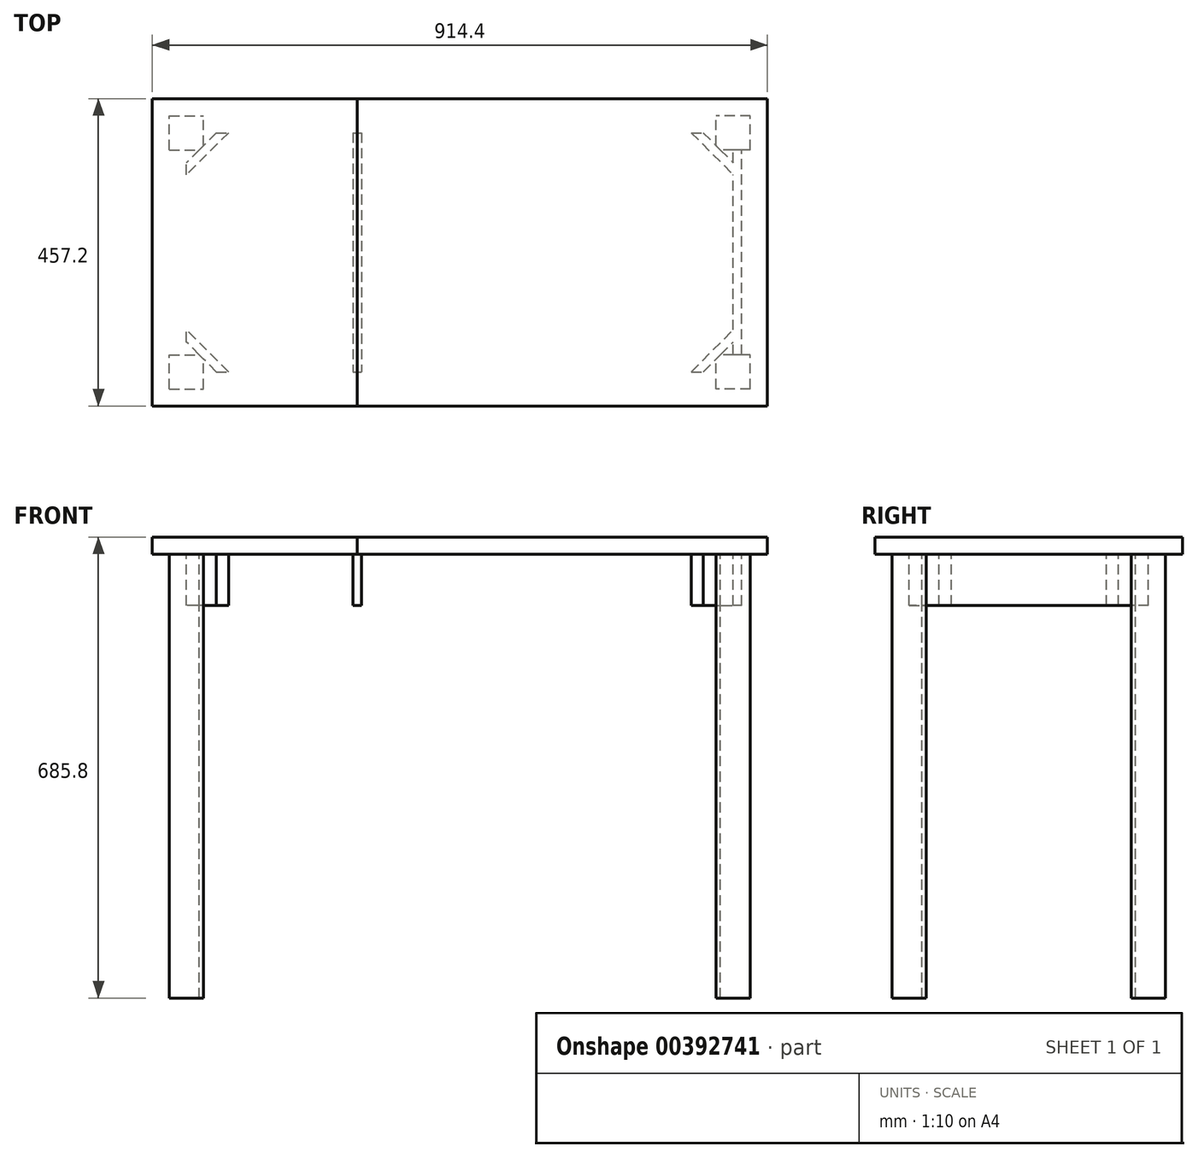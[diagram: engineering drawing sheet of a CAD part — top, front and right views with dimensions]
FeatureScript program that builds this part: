
annotation { "Feature Type Name" : "Feature", "Feature Type Description" : "" }
export const myFeature = defineFeature(function(context is Context, id is Id, definition is map)
    precondition{}
    {
        {
            var Q0;
            Q0=qCreatedBy(makeId("Top.planeOp"),FACE);
            var sketch = newSketch(context, id + "F0", { "sketchPlane" : qUnion([Q0])});
            skLineSegment(sketch, "E0.bottom", {"start": v(-394.13, 238.74) * mm, "end": v(215.47, 238.74) * mm});
            skLineSegment(sketch, "E0.top", {"start": v(-394.13, -218.46) * mm, "end": v(215.47, -218.46) * mm});
            skLineSegment(sketch, "E0.left", {"start": v(-394.13, 238.74) * mm, "end": v(-394.13, -218.46) * mm});
            skLineSegment(sketch, "E0.right", {"start": v(215.47, 238.74) * mm, "end": v(215.47, -218.46) * mm});
            skLineSegment(sketch, "E1.bottom", {"start": v(-394.13, 238.74) * mm, "end": v(-698.93, 238.74) * mm});
            skLineSegment(sketch, "E1.top", {"start": v(-394.13, -218.46) * mm, "end": v(-698.93, -218.46) * mm});
            skLineSegment(sketch, "E1.right", {"start": v(-698.93, 238.74) * mm, "end": v(-698.93, -218.46) * mm});
            skSolve(sketch);
        }
        {
            var Q0;
            Q0=makeQuery(id+"F0.imprint","IMPRINT",FACE,{"disambiguationData":[TD([[makeQuery(id+"F0.imprint","IMPRINT",EDGE,{"derivedFrom":sQuery(id+"F0.wireOp",EDGE,"E0.bottom")}),-1.0]])]});
            extrude(context, id + "F1", {"entities" : qUnion([Q0]), "depth" : 25.4 * mm});
        }
        {
            var Q0;
            Q0=makeQuery(id+"F0.imprint","IMPRINT",FACE,{"disambiguationData":[TD([[makeQuery(id+"F0.imprint","IMPRINT",EDGE,{"derivedFrom":sQuery(id+"F0.wireOp",EDGE,"E1.bottom")}),1.0]])]});
            extrude(context, id + "F2", {"entities" : qUnion([Q0]), "depth" : 25.4 * mm});
        }
        {
            var Q0;
            Q0=makeQuery(id+"F0.imprint","IMPRINT",FACE,{"disambiguationData":[TD([[makeQuery(id+"F0.imprint","IMPRINT",EDGE,{"derivedFrom":sQuery(id+"F0.wireOp",EDGE,"E0.bottom")}),-1.0]])]});
            var sketch = newSketch(context, id + "F3", { "sketchPlane" : qUnion([Q0])});
            skLineSegment(sketch, "E2.bottom", {"start": v(-673.53, -193.06) * mm, "end": v(-622.73, -193.06) * mm});
            skLineSegment(sketch, "E2.top", {"start": v(-673.53, -142.26) * mm, "end": v(-622.73, -142.26) * mm});
            skLineSegment(sketch, "E2.left", {"start": v(-673.53, -193.06) * mm, "end": v(-673.53, -142.26) * mm});
            skLineSegment(sketch, "E2.right", {"start": v(-622.73, -193.06) * mm, "end": v(-622.73, -142.26) * mm});
            skLineSegment(sketch, "E3.bottom", {"start": v(-673.53, 162.54) * mm, "end": v(-622.73, 162.54) * mm});
            skLineSegment(sketch, "E3.top", {"start": v(-673.53, 213.34) * mm, "end": v(-622.73, 213.34) * mm});
            skLineSegment(sketch, "E3.left", {"start": v(-673.53, 162.54) * mm, "end": v(-673.53, 213.34) * mm});
            skLineSegment(sketch, "E3.right", {"start": v(-622.73, 162.54) * mm, "end": v(-622.73, 213.34) * mm});
            skLineSegment(sketch, "E4.bottom", {"start": v(-648.13, -142.26) * mm, "end": v(-660.83, -142.26) * mm});
            skLineSegment(sketch, "E4.top", {"start": v(-648.13, 162.54) * mm, "end": v(-660.83, 162.54) * mm});
            skLineSegment(sketch, "E4.left", {"start": v(-648.13, -142.26) * mm, "end": v(-648.13, 162.54) * mm});
            skLineSegment(sketch, "E4.right", {"start": v(-660.83, -142.26) * mm, "end": v(-660.83, 162.54) * mm});
            skLineSegment(sketch, "E5", {"start": v(-241.73, -218.46) * mm, "end": v(-241.73, 238.74) * mm, "construction": true});
            skLineSegment(sketch, "E6.MirrorCS", {"start": v(190.07, -193.06) * mm, "end": v(139.27, -193.06) * mm});
            skLineSegment(sketch, "E7.MirrorCS", {"start": v(190.07, -193.06) * mm, "end": v(190.07, -142.26) * mm});
            skLineSegment(sketch, "E8.MirrorCS", {"start": v(190.07, -142.26) * mm, "end": v(139.27, -142.26) * mm});
            skLineSegment(sketch, "E9.MirrorCS", {"start": v(139.27, -193.06) * mm, "end": v(139.27, -142.26) * mm});
            skLineSegment(sketch, "E10.MirrorCS", {"start": v(164.67, -142.26) * mm, "end": v(164.67, 162.54) * mm});
            skLineSegment(sketch, "E11.MirrorCS", {"start": v(177.37, -142.26) * mm, "end": v(177.37, 162.54) * mm});
            skLineSegment(sketch, "E12.MirrorCS", {"start": v(190.07, 162.54) * mm, "end": v(139.27, 162.54) * mm});
            skLineSegment(sketch, "E13.MirrorCS", {"start": v(139.27, 162.54) * mm, "end": v(139.27, 213.34) * mm});
            skLineSegment(sketch, "E14.MirrorCS", {"start": v(190.07, 213.34) * mm, "end": v(139.27, 213.34) * mm});
            skLineSegment(sketch, "E15.MirrorCS", {"start": v(190.07, 162.54) * mm, "end": v(190.07, 213.34) * mm});
            skLineSegment(sketch, "E16", {"start": v(-622.73, -167.66) * mm, "end": v(-241.73, -167.66) * mm});
            skLineSegment(sketch, "E17", {"start": v(-241.73, -167.66) * mm, "end": v(139.27, -167.66) * mm});
            skLineSegment(sketch, "E18", {"start": v(139.27, -167.66) * mm, "end": v(139.27, -180.36) * mm});
            skLineSegment(sketch, "E19", {"start": v(139.27, -180.36) * mm, "end": v(-622.73, -180.36) * mm});
            skLineSegment(sketch, "E20", {"start": v(-622.73, -180.36) * mm, "end": v(-622.73, -167.66) * mm});
            skLineSegment(sketch, "E21", {"start": v(-603.68, -167.66) * mm, "end": v(-648.13, -123.2) * mm});
            skLineSegment(sketch, "E22", {"start": v(-585.72, -167.66) * mm, "end": v(-648.13, -105.25) * mm});
            skLineSegment(sketch, "E23.MirrorCS", {"start": v(102.26, -167.66) * mm, "end": v(164.67, -105.25) * mm});
            skLineSegment(sketch, "E24.MirrorCS", {"start": v(120.22, -167.66) * mm, "end": v(164.67, -123.2) * mm});
            skPoint(sketch, "E25", {"position": v(-622.73, -148.6) * mm});
            skPoint(sketch, "E26", {"position": v(-629.08, -142.26) * mm});
            skLineSegment(sketch, "E27.bottom", {"start": v(-622.73, 187.94) * mm, "end": v(139.27, 187.94) * mm});
            skLineSegment(sketch, "E27.top", {"start": v(-622.73, 200.64) * mm, "end": v(139.27, 200.64) * mm});
            skLineSegment(sketch, "E27.left", {"start": v(-622.73, 187.94) * mm, "end": v(-622.73, 200.64) * mm});
            skLineSegment(sketch, "E27.right", {"start": v(139.27, 187.94) * mm, "end": v(139.27, 200.64) * mm});
            skLineSegment(sketch, "E28", {"start": v(215.47, 10.14) * mm, "end": v(-698.93, 10.14) * mm, "construction": true});
            skLineSegment(sketch, "E29.MirrorCS", {"start": v(102.26, 187.94) * mm, "end": v(164.67, 125.53) * mm});
            skLineSegment(sketch, "E30.MirrorCS", {"start": v(120.22, 187.94) * mm, "end": v(164.67, 143.5) * mm});
            skLineSegment(sketch, "E31.MirrorCS", {"start": v(-585.72, 187.94) * mm, "end": v(-648.13, 125.53) * mm});
            skLineSegment(sketch, "E32.MirrorCS", {"start": v(-603.68, 187.94) * mm, "end": v(-648.13, 143.5) * mm});
            skLineSegment(sketch, "E33.bottom", {"start": v(-400.91, 187.94) * mm, "end": v(-388.21, 187.94) * mm});
            skLineSegment(sketch, "E33.top", {"start": v(-400.91, -167.66) * mm, "end": v(-388.21, -167.66) * mm});
            skLineSegment(sketch, "E33.left", {"start": v(-400.91, 187.94) * mm, "end": v(-400.91, -167.66) * mm});
            skLineSegment(sketch, "E33.right", {"start": v(-388.21, 187.94) * mm, "end": v(-388.21, -167.66) * mm});
            skSolve(sketch);
        }
        {
            var Q0;
            {var subQ0=sQuery(id+"F3.wireOp",EDGE,"E18");Q0=makeQuery(id+"F3.imprint","IMPRINT",FACE,{"disambiguationData":[TD([[makeQuery(id+"F3.imprint","IMPRINT",EDGE,{"derivedFrom":subQ0}),-1.0]])]});}
            var Q1;
            {var subQ0=sQuery(id+"F3.wireOp",EDGE,"E20");Q1=makeQuery(id+"F3.imprint","IMPRINT",FACE,{"disambiguationData":[TD([[makeQuery(id+"F3.imprint","IMPRINT",EDGE,{"derivedFrom":subQ0}),-1.0]])]});}
            var Q2;
            {var subQ3=sQuery(id+"F3.wireOp",EDGE,"E22");Q2=makeQuery(id+"F3.imprint","IMPRINT",FACE,{"disambiguationData":[TD([[makeQuery(id+"F3.imprint","IMPRINT",EDGE,{"derivedFrom":subQ3}),1.0]])]});}
            var Q3;
            {var subQ3=sQuery(id+"F3.wireOp",EDGE,"E4.bottom");Q3=makeQuery(id+"F3.imprint","IMPRINT",FACE,{"disambiguationData":[TD([[makeQuery(id+"F3.imprint","IMPRINT",EDGE,{"derivedFrom":subQ3}),-1.0]])]});}
            var Q4;
            {var subQ0=sQuery(id+"F3.wireOp",EDGE,"E31.MirrorCS");Q4=makeQuery(id+"F3.imprint","IMPRINT",FACE,{"disambiguationData":[TD([[makeQuery(id+"F3.imprint","IMPRINT",EDGE,{"derivedFrom":subQ0}),-1.0]])]});}
            var Q5;
            {var subQ6=sQuery(id+"F3.wireOp",EDGE,"E27.left");Q5=makeQuery(id+"F3.imprint","IMPRINT",FACE,{"disambiguationData":[TD([[makeQuery(id+"F3.imprint","IMPRINT",EDGE,{"derivedFrom":subQ6}),-1.0]])]});}
            var Q6;
            {var subQ0=sQuery(id+"F3.wireOp",EDGE,"E27.right");Q6=makeQuery(id+"F3.imprint","IMPRINT",FACE,{"disambiguationData":[TD([[makeQuery(id+"F3.imprint","IMPRINT",EDGE,{"derivedFrom":subQ0}),1.0]])]});}
            var Q7;
            {var subQ6=sQuery(id+"F3.wireOp",EDGE,"E29.MirrorCS");Q7=makeQuery(id+"F3.imprint","IMPRINT",FACE,{"disambiguationData":[TD([[makeQuery(id+"F3.imprint","IMPRINT",EDGE,{"derivedFrom":subQ6}),1.0]])]});}
            var Q8;
            {var subQ6=sQuery(id+"F3.wireOp",EDGE,"E11.MirrorCS");Q8=makeQuery(id+"F3.imprint","IMPRINT",FACE,{"disambiguationData":[TD([[makeQuery(id+"F3.imprint","IMPRINT",EDGE,{"derivedFrom":subQ6}),1.0]])]});}
            var Q9;
            {var subQ0=sQuery(id+"F3.wireOp",EDGE,"E2.right");var subQ1=sQuery(id+"F3.wireOp",EDGE,"E2.top");var subQ2=makeQuery(id+"F3.imprint","INTERSECT",VERTEX,{"derivedFrom":[subQ1,subQ0]});Q9=makeQuery(id+"F3.imprint","IMPRINT",FACE,{"disambiguationData":[TD([[makeQuery(id+"F3.imprint","IMPRINT",EDGE,{"disambiguationData":[TD([[subQ2,1.0]])],"derivedFrom":subQ1}),-1.0]])]});}
            var Q10;
            {var subQ0=sQuery(id+"F3.wireOp",EDGE,"E3.right");var subQ1=sQuery(id+"F3.wireOp",EDGE,"E3.bottom");var subQ2=makeQuery(id+"F3.imprint","INTERSECT",VERTEX,{"derivedFrom":[subQ1,subQ0]});Q10=makeQuery(id+"F3.imprint","IMPRINT",FACE,{"disambiguationData":[TD([[makeQuery(id+"F3.imprint","IMPRINT",EDGE,{"disambiguationData":[TD([[subQ2,1.0]])],"derivedFrom":subQ1}),1.0]])]});}
            var Q11;
            {var subQ0=sQuery(id+"F3.wireOp",EDGE,"E13.MirrorCS");var subQ1=sQuery(id+"F3.wireOp",EDGE,"E12.MirrorCS");var subQ2=makeQuery(id+"F3.imprint","INTERSECT",VERTEX,{"derivedFrom":[subQ1,subQ0]});Q11=makeQuery(id+"F3.imprint","IMPRINT",FACE,{"disambiguationData":[TD([[makeQuery(id+"F3.imprint","IMPRINT",EDGE,{"disambiguationData":[TD([[subQ2,1.0]])],"derivedFrom":subQ1}),-1.0]])]});}
            var Q12;
            {var subQ0=sQuery(id+"F3.wireOp",EDGE,"E9.MirrorCS");var subQ1=sQuery(id+"F3.wireOp",EDGE,"E8.MirrorCS");var subQ2=makeQuery(id+"F3.imprint","INTERSECT",VERTEX,{"derivedFrom":[subQ1,subQ0]});Q12=makeQuery(id+"F3.imprint","IMPRINT",FACE,{"disambiguationData":[TD([[makeQuery(id+"F3.imprint","IMPRINT",EDGE,{"disambiguationData":[TD([[subQ2,1.0]])],"derivedFrom":subQ1}),1.0]])]});}
            var Q13;
            {var subQ0=sQuery(id+"F3.wireOp",EDGE,"E23.MirrorCS");Q13=makeQuery(id+"F3.imprint","IMPRINT",FACE,{"disambiguationData":[TD([[makeQuery(id+"F3.imprint","IMPRINT",EDGE,{"derivedFrom":subQ0}),-1.0]])]});}
            var Q14;
            {var subQ0=sQuery(id+"F3.wireOp",EDGE,"E33.left");Q14=makeQuery(id+"F3.imprint","IMPRINT",FACE,{"disambiguationData":[TD([[makeQuery(id+"F3.imprint","IMPRINT",EDGE,{"derivedFrom":subQ0}),1.0]])]});}
            var Q15;
            {var subQ0=sQuery(id+"F3.wireOp",EDGE,"E33.right");Q15=makeQuery(id+"F3.imprint","IMPRINT",FACE,{"disambiguationData":[TD([[makeQuery(id+"F3.imprint","IMPRINT",EDGE,{"derivedFrom":subQ0}),-1.0]])]});}
            extrude(context, id + "F4", {"entities" : qUnion([Q0, Q1, Q2, Q3, Q4, Q5, Q6, Q7, Q8, Q9, Q10, Q11, Q12, Q13, Q14, Q15]), "depth" : -76.2 * mm});
        }
        {
            var Q0;
            {var subQ9=sQuery(id+"F3.wireOp",EDGE,"E14.MirrorCS");Q0=makeQuery(id+"F3.imprint","IMPRINT",FACE,{"disambiguationData":[TD([[makeQuery(id+"F3.imprint","IMPRINT",EDGE,{"derivedFrom":subQ9}),1.0]])]});}
            var Q1;
            {var subQ4=sQuery(id+"F3.wireOp",EDGE,"E6.MirrorCS");Q1=makeQuery(id+"F3.imprint","IMPRINT",FACE,{"disambiguationData":[TD([[makeQuery(id+"F3.imprint","IMPRINT",EDGE,{"derivedFrom":subQ4}),-1.0]])]});}
            var Q2;
            {var subQ1=sQuery(id+"F3.wireOp",EDGE,"E3.top");Q2=makeQuery(id+"F3.imprint","IMPRINT",FACE,{"disambiguationData":[TD([[makeQuery(id+"F3.imprint","IMPRINT",EDGE,{"derivedFrom":subQ1}),-1.0]])]});}
            var Q3;
            {var subQ5=sQuery(id+"F3.wireOp",EDGE,"E2.bottom");Q3=makeQuery(id+"F3.imprint","IMPRINT",FACE,{"disambiguationData":[TD([[makeQuery(id+"F3.imprint","IMPRINT",EDGE,{"derivedFrom":subQ5}),1.0]])]});}
            extrude(context, id + "F5", {"entities" : qUnion([Q0, Q1, Q2, Q3]), "operationType" : NewBodyOperationType.ADD, "depth" : -660.4 * mm});
        }
    });
